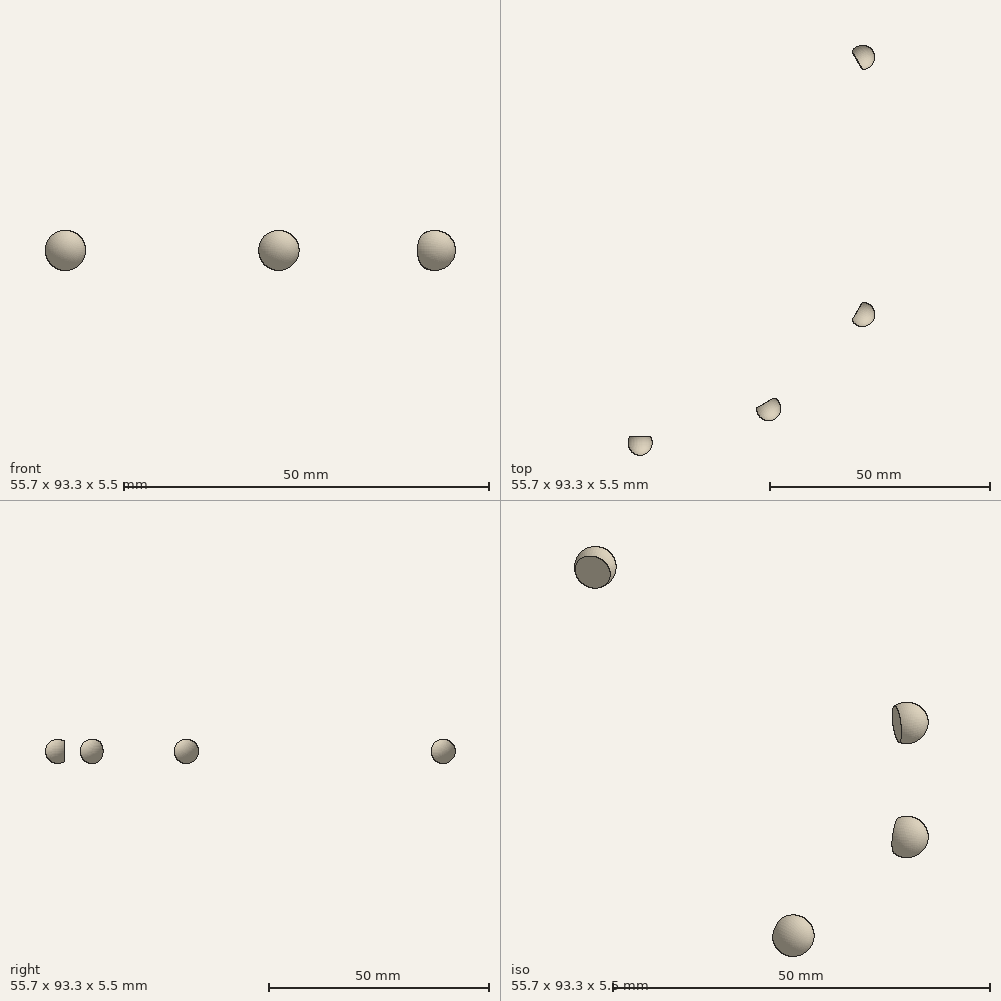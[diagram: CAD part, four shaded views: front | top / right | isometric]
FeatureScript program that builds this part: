
annotation { "Feature Type Name" : "Feature", "Feature Type Description" : "" }
export const myFeature = defineFeature(function(context is Context, id is Id, definition is map)
    precondition{}
    {
        {
            var Q0;
            Q0=qCreatedBy(makeId("Top.planeOp"),FACE);
            var sketch = newSketch(context, id + "F0", { "sketchPlane" : qUnion([Q0])});
            skCircle(sketch, "E0", {"center": v(-1.5, -3.2) * mm, "radius": 60.33 * mm});
            skCircle(sketch, "E1", {"center": v(-1.5, -3.2) * mm, "radius": 57.15 * mm});
            skSolve(sketch);
        }
        {
            var Q0;
            Q0 = qSketchRegion(id + "F0", true);
            extrude(context, id + "F1", {"entities" : qUnion([Q0]), "depth" : 50.8 * mm});
        }
        {
            var Q0;
            Q0=qCreatedBy(makeId("Front.planeOp"),FACE);
            var sketch = newSketch(context, id + "F2", { "sketchPlane" : qUnion([Q0])});
            skLineSegment(sketch, "E2", {"start": v(-61.76, 50.86) * mm, "end": v(58.59, 50.86) * mm});
            skArc(sketch, "E3", {"start": v(-27.24, 27.98) * mm, "mid": v(-10.73, 35.28) * mm, "end": v(-1.59, 50.86) * mm});
            skLineSegment(sketch, "E4", {"start": v(-27.24, 27.98) * mm, "end": v(-71.41, 27.98) * mm});
            skLineSegment(sketch, "E5", {"start": v(-71.41, 27.98) * mm, "end": v(-61.76, 50.86) * mm});
            skSolve(sketch);
        }
        {
            var Q0;
            Q0 = qSketchRegion(id + "F2", true);
            extrude(context, id + "F3", {"entities" : qUnion([Q0]), "operationType" : NewBodyOperationType.REMOVE, "depth" : 68.51 * mm, "hasSecondDirection" : true, "secondDirectionOppositeDirection" : true, "secondDirectionDepth" : 71.55 * mm});
        }
        {
            var Q0;
            Q0=qCreatedBy(makeId("Front.planeOp"),FACE);
            var sketch = newSketch(context, id + "F4", { "sketchPlane" : qUnion([Q0])});
            skLineSegment(sketch, "E6.bottom", {"start": v(-68.64, 54.96) * mm, "end": v(-49.46, 54.96) * mm});
            skLineSegment(sketch, "E6.top", {"start": v(-68.64, 43.72) * mm, "end": v(-49.46, 43.72) * mm});
            skLineSegment(sketch, "E6.left", {"start": v(-68.64, 54.96) * mm, "end": v(-68.64, 43.72) * mm});
            skLineSegment(sketch, "E6.right", {"start": v(-49.46, 54.96) * mm, "end": v(-49.46, 43.72) * mm});
            skSolve(sketch);
        }
        {
            var Q0;
            Q0 = qSketchRegion(id + "F4", true);
            extrude(context, id + "F5", {"entities" : qUnion([Q0]), "operationType" : NewBodyOperationType.REMOVE, "depth" : 25.4 * mm});
        }
        {
            var Q0;
            Q0=qCreatedBy(makeId("Front.planeOp"),FACE);
            var sketch = newSketch(context, id + "F6", { "sketchPlane" : qUnion([Q0])});
            skLineSegment(sketch, "E7", {"start": v(-1.59, 50.56) * mm, "end": v(-1.59, 56.02) * mm});
            skLineSegment(sketch, "E8", {"start": v(-1.59, 56.02) * mm, "end": v(66.65, 56.02) * mm});
            skLineSegment(sketch, "E9", {"start": v(58.85, 27.85) * mm, "end": v(66.65, 56.02) * mm});
            skLineSegment(sketch, "E10", {"start": v(-1.59, 50.56) * mm, "end": v(-1.59, -5.61) * mm});
            skLineSegment(sketch, "E11", {"start": v(58.85, 27.85) * mm, "end": v(65.73, -4.29) * mm});
            skLineSegment(sketch, "E12", {"start": v(-1.59, -5.61) * mm, "end": v(65.73, -4.29) * mm});
            skSolve(sketch);
        }
        {
            var Q0;
            Q0 = qSketchRegion(id + "F6", true);
            extrude(context, id + "F7", {"entities" : qUnion([Q0]), "operationType" : NewBodyOperationType.REMOVE, "oppositeDirection" : true, "depth" : 62.56 * mm, "hasSecondDirection" : true, "secondDirectionOppositeDirection" : false, "secondDirectionDepth" : 75.26 * mm});
        }
        {
            var Q0;
            Q0=makeQuery(id+"F3.boolean.opBoolean","SPLIT",BODY,{"disambiguationData":[OD(1.0)],"derivedFrom":makeQuery(id+"F1.opExtrude","SWEPT_BODY",BODY,{"disambiguationData":[OSD([sQuery(id+"F0.wireOp",EDGE,"E0"),sQuery(id+"F0.wireOp",EDGE,"E1")])]})});
            var Q1;
            Q1=makeQuery(id+"F7.boolean.opBoolean","COPY",FACE,{"disambiguationData":[OD(0.0)],"derivedFrom":makeQuery(id+"F7.opExtrude","SWEPT_FACE",FACE,{"disambiguationData":[OSD([sQuery(id+"F6.wireOp",EDGE,"E7"),sQuery(id+"F6.wireOp",EDGE,"E10")])]})});
            mirror(context, id + "F8", {"operationType" : NewBodyOperationType.ADD, "entities" : qUnion([Q0]), "mirrorPlane" : qUnion([Q1])});
        }
        {
            var Q0;
            Q0=makeQuery(id+"F3.boolean.opBoolean","SPLIT",BODY,{"disambiguationData":[OD(1.0)],"derivedFrom":makeQuery(id+"F1.opExtrude","SWEPT_BODY",BODY,{"disambiguationData":[OSD([sQuery(id+"F0.wireOp",EDGE,"E0"),sQuery(id+"F0.wireOp",EDGE,"E1")])]})});
            var Q1;
            Q1=makeQuery(id+"F3.boolean.opBoolean","INTERSECT",EDGE,{"derivedFrom":[makeQuery(id+"F1.opExtrude","SWEPT_FACE",FACE,{"disambiguationData":[OSD([sQuery(id+"F0.wireOp",EDGE,"E0")])]}),makeQuery(id+"F3.opExtrude","SWEPT_FACE",FACE,{"disambiguationData":[OSD([sQuery(id+"F2.wireOp",EDGE,"E4")])]})]});
            circularPattern(context, id + "F9", {"operationType" : NewBodyOperationType.ADD, "entities" : qUnion([Q0]), "axis" : qUnion([Q1]), "angle" : 30 * degree, "instanceCount" : 6});
        }
        {
            var Q0;
            Q0=qCreatedBy(makeId("Top.planeOp"),FACE);
            cPlane(context, id + "F10", {"entities" : qUnion([Q0]), "cplaneType" : CPlaneType.OFFSET, "offset" : 50.8 * mm, "width" : 152.4 * mm, "height" : 152.4 * mm});
        }
        {
            var Q0;
            Q0=qCreatedBy(id+"F10.planeOp",FACE);
            var sketch = newSketch(context, id + "F11", { "sketchPlane" : qUnion([Q0])});
            skCircle(sketch, "E13", {"center": v(-60.14, -3.32) * mm, "radius": 2.84 * mm});
            skLineSegment(sketch, "E14", {"start": v(-57.3, -3.24) * mm, "end": v(-62.98, -3.24) * mm});
            skSolve(sketch);
        }
        {
            var Q0;
            {var subQ0=sQuery(id+"F11.wireOp",EDGE,"E14");Q0=makeQuery(id+"F11.imprint","IMPRINT",FACE,{"disambiguationData":[TD([[makeQuery(id+"F11.imprint","IMPRINT",EDGE,{"derivedFrom":subQ0}),-1.0]])]});}
            var Q1;
            Q1=sQuery(id+"F11.wireOp",EDGE,"E14");
            revolve(context, id + "F12", {"entities" : qUnion([Q0]), "axis" : qUnion([Q1]), "revolveType" : RevolveType.FULL});
        }
        {
            var Q0;
            Q0=makeQuery(id+"F12.opRevolve","SWEPT_BODY",BODY,{"disambiguationData":[OSD([sQuery(id+"F11.wireOp",EDGE,"E13"),sQuery(id+"F11.wireOp",EDGE,"E14")])]});
            var Q1;
            {var subQ0=sQuery(id+"F0.wireOp",EDGE,"E1");var subQ1=makeQuery(id+"F1.opExtrude","SWEPT_FACE",FACE,{"disambiguationData":[OSD([subQ0])]});var subQ2=subQ1;var subQ3=makeQuery(id+"F8.opPattern","COPY",FACE,{"derivedFrom":subQ2,"instanceName":"1"});var subQ4=sQuery(id+"F0.wireOp",EDGE,"E0");var subQ5=makeQuery(id+"F1.opExtrude","CAP_FACE",FACE,{"disambiguationData":[OSD([subQ4,subQ0])],"isStart":true});var subQ6=subQ5;var subQ7=makeQuery(id+"F8.opPattern","COPY",FACE,{"derivedFrom":subQ6,"instanceName":"1"});var subQ8=makeQuery(id+"F8.boolean.opBoolean","MERGE",FACE,{"derivedFrom":[subQ6,subQ7]});var subQ9=makeQuery(id+"F3.opExtrude","SWEPT_FACE",FACE,{"disambiguationData":[OSD([sQuery(id+"F2.wireOp",EDGE,"E3")])]});var subQ10=makeQuery(id+"F3.boolean.opBoolean","COPY",FACE,{"disambiguationData":[OD(1.0)],"derivedFrom":subQ9});var subQ11=makeQuery(id+"F8.opPattern","COPY",FACE,{"derivedFrom":makeQuery(id+"F3.boolean.opBoolean","COPY",FACE,{"derivedFrom":makeQuery(id+"F3.opExtrude","SWEPT_FACE",FACE,{"disambiguationData":[OSD([sQuery(id+"F2.wireOp",EDGE,"E4")])]})}),"instanceName":"1"});var subQ12=makeQuery(id+"F1.opExtrude","CAP_FACE",FACE,{"disambiguationData":[OSD([subQ4,subQ0])],"isStart":false});Q1=makeQuery(id+"F9.boolean.opBoolean","SPLIT",FACE,{"disambiguationData":[TD([subQ5,subQ12,subQ1,subQ11,makeQuery(id+"F8.opPattern","COPY",FACE,{"derivedFrom":subQ10,"instanceName":"1"}),subQ7,makeQuery(id+"F8.opPattern","COPY",FACE,{"derivedFrom":makeQuery(id+"F7.boolean.opBoolean","SPLIT",FACE,{"disambiguationData":[TD([subQ10])],"derivedFrom":makeQuery(id+"F3.boolean.opBoolean","SPLIT",FACE,{"disambiguationData":[TD([subQ1])],"derivedFrom":subQ12})}),"instanceName":"1"}),makeQuery(id+"F9.opPattern","COPY",FACE,{"derivedFrom":subQ2,"instanceName":"1"}),makeQuery(id+"F9.opPattern","COPY",FACE,{"derivedFrom":subQ11,"instanceName":"1"}),makeQuery(id+"F9.opPattern","COPY",FACE,{"derivedFrom":subQ3,"instanceName":"1"}),makeQuery(id+"F9.opPattern","COPY",FACE,{"derivedFrom":subQ8,"instanceName":"1"}),makeQuery(id+"F9.opPattern","COPY",FACE,{"derivedFrom":subQ2,"instanceName":"2"}),makeQuery(id+"F9.opPattern","COPY",FACE,{"derivedFrom":subQ11,"instanceName":"2"}),makeQuery(id+"F9.opPattern","COPY",FACE,{"derivedFrom":subQ8,"instanceName":"2"}),makeQuery(id+"F9.opPattern","COPY",FACE,{"derivedFrom":subQ2,"instanceName":"3"}),makeQuery(id+"F9.opPattern","COPY",FACE,{"derivedFrom":subQ11,"instanceName":"3"}),makeQuery(id+"F9.opPattern","COPY",FACE,{"derivedFrom":subQ8,"instanceName":"3"}),makeQuery(id+"F9.opPattern","COPY",FACE,{"derivedFrom":subQ2,"instanceName":"4"}),makeQuery(id+"F9.opPattern","COPY",FACE,{"derivedFrom":subQ11,"instanceName":"4"}),makeQuery(id+"F9.opPattern","COPY",FACE,{"derivedFrom":subQ8,"instanceName":"4"}),makeQuery(id+"F9.opPattern","COPY",FACE,{"derivedFrom":subQ2,"instanceName":"5"}),makeQuery(id+"F9.opPattern","COPY",FACE,{"derivedFrom":subQ11,"instanceName":"5"}),makeQuery(id+"F9.opPattern","COPY",FACE,{"derivedFrom":subQ8,"instanceName":"5"})])],"derivedFrom":subQ3});}
            circularPattern(context, id + "F13", {"operationType" : NewBodyOperationType.ADD, "entities" : qUnion([Q0]), "axis" : qUnion([Q1]), "angle" : 30 * degree, "instanceCount" : 12});
        }
        {
            var Q0;
            Q0=qCreatedBy(makeId("Right.planeOp"),FACE);
            cPlane(context, id + "F14", {"entities" : qUnion([Q0]), "cplaneType" : CPlaneType.OFFSET, "offset" : 1.65 * mm, "oppositeDirection" : true, "width" : 152.4 * mm, "height" : 152.4 * mm});
        }
        {
            var Q0;
            Q0=qCreatedBy(id+"F14.planeOp",FACE);
            var sketch = newSketch(context, id + "F15", { "sketchPlane" : qUnion([Q0])});
            skLineSegment(sketch, "E15", {"start": v(-3.04, 29) * mm, "end": v(-13.92, 18.12) * mm});
            skLineSegment(sketch, "E16", {"start": v(-3.04, 29) * mm, "end": v(7.83, 18.12) * mm});
            skLineSegment(sketch, "E17", {"start": v(-13.92, 18.12) * mm, "end": v(-3.04, 7.25) * mm});
            skLineSegment(sketch, "E18", {"start": v(7.83, 18.12) * mm, "end": v(-3.04, 7.25) * mm});
            skLineSegment(sketch, "E19", {"start": v(-3.04, 29) * mm, "end": v(-3.04, 7.25) * mm});
            skLineSegment(sketch, "E20", {"start": v(-13.92, 18.12) * mm, "end": v(7.83, 18.12) * mm});
            skSolve(sketch);
        }
        {
            var Q0;
            Q0 = qSketchRegion(id + "F15", true);
            extrude(context, id + "F16", {"entities" : qUnion([Q0]), "depth" : 60.96 * mm, "hasSecondDirection" : true, "secondDirectionOppositeDirection" : true, "secondDirectionDepth" : 60.96 * mm});
        }
        {
            var Q0;
            {var subQ0=makeQuery(id+"F1.opExtrude","CAP_FACE",FACE,{"disambiguationData":[OSD([sQuery(id+"F0.wireOp",EDGE,"E0"),sQuery(id+"F0.wireOp",EDGE,"E1")])],"isStart":true});var subQ1=makeQuery(id+"F8.boolean.opBoolean","MERGE",FACE,{"derivedFrom":[subQ0,makeQuery(id+"F8.opPattern","COPY",FACE,{"derivedFrom":subQ0,"instanceName":"1"})]});Q0=makeQuery(id+"F9.boolean.opBoolean","MERGE",FACE,{"derivedFrom":[subQ1,makeQuery(id+"F9.opPattern","COPY",FACE,{"derivedFrom":subQ1,"instanceName":"1"}),makeQuery(id+"F9.opPattern","COPY",FACE,{"derivedFrom":subQ1,"instanceName":"2"}),makeQuery(id+"F9.opPattern","COPY",FACE,{"derivedFrom":subQ1,"instanceName":"3"}),makeQuery(id+"F9.opPattern","COPY",FACE,{"derivedFrom":subQ1,"instanceName":"4"}),makeQuery(id+"F9.opPattern","COPY",FACE,{"derivedFrom":subQ1,"instanceName":"5"})]});}
            var sketch = newSketch(context, id + "F17", { "sketchPlane" : qUnion([Q0])});
            skSolve(sketch);
        }
        {
            var Q0;
            Q0 = qSketchRegion(id + "F17", true);
            var Q1;
            {var subQ0=makeQuery(id+"F1.opExtrude","CAP_EDGE",EDGE,{"disambiguationData":[OSD([sQuery(id+"F0.wireOp",EDGE,"E1")])],"isStart":true});Q1=makeQuery(id+"F17.imprint","IMPRINT",FACE,{"disambiguationData":[TD([[makeQuery(id+"F17.imprint","IMPRINT",EDGE,{"derivedFrom":subQ0}),-1.0]])]});}
            extrude(context, id + "F18", {"entities" : qUnion([Q0, Q1]), "operationType" : NewBodyOperationType.REMOVE, "oppositeDirection" : true, "depth" : 101.6 * mm});
        }
        {
            var Q0;
            Q0=makeQuery(id+"F16.opExtrude","CAP_FACE",FACE,{"disambiguationData":[OSD([sQuery(id+"F15.wireOp",EDGE,"E15"),sQuery(id+"F15.wireOp",EDGE,"E16"),sQuery(id+"F15.wireOp",EDGE,"E17"),sQuery(id+"F15.wireOp",EDGE,"E18")])],"isStart":true});
            var sketch = newSketch(context, id + "F19", { "sketchPlane" : qUnion([Q0])});
            skLineSegment(sketch, "E21", {"start": v(3.04, 29) * mm, "end": v(3.04, 7.25) * mm});
            skLineSegment(sketch, "E22", {"start": v(-7.83, 18.12) * mm, "end": v(13.92, 18.12) * mm});
            skSolve(sketch);
        }
        {
            var Q0;
            {var subQ3=makeQuery(id+"F16.opExtrude","CAP_EDGE",EDGE,{"disambiguationData":[OSD([sQuery(id+"F15.wireOp",EDGE,"E16")])],"isStart":true});Q0=makeQuery(id+"F19.imprint","IMPRINT",FACE,{"disambiguationData":[TD([[makeQuery(id+"F19.imprint","IMPRINT",EDGE,{"derivedFrom":subQ3}),1.0]])]});}
            cPlane(context, id + "F20", {"entities" : qUnion([Q0]), "cplaneType" : CPlaneType.OFFSET, "offset" : 2.54 * mm, "width" : 152.4 * mm, "height" : 152.4 * mm});
        }
        {
            var Q0;
            Q0=qCreatedBy(id+"F20.planeOp",FACE);
            var sketch = newSketch(context, id + "F21", { "sketchPlane" : qUnion([Q0])});
            skPoint(sketch, "E23", {"position": v(3.07, 18.1) * mm});
            skSolve(sketch);
        }
        {
            var Q1;
            Q1=sQuery(id+"F21.wireOp",VERTEX,"E23");
            var Q2;
            Q2=makeQuery(id+"F16.opExtrude","CAP_FACE",FACE,{"disambiguationData":[OSD([sQuery(id+"F15.wireOp",EDGE,"E15"),sQuery(id+"F15.wireOp",EDGE,"E16"),sQuery(id+"F15.wireOp",EDGE,"E17"),sQuery(id+"F15.wireOp",EDGE,"E18")])],"isStart":true});
            loft(context, id + "F22", {"operationType" : NewBodyOperationType.ADD, "sheetProfilesArray" : [{ "sheetProfileEntities" : qUnion([Q1]) }, { "sheetProfileEntities" : qUnion([Q2]) }]});
        }
        {
            var Q0;
            Q0=makeQuery(id+"F18.boolean.opBoolean","SPLIT",BODY,{"disambiguationData":[OD(0.0)],"derivedFrom":makeQuery(id+"F16.opExtrude","SWEPT_BODY",BODY,{"disambiguationData":[OSD([sQuery(id+"F15.wireOp",EDGE,"E15"),sQuery(id+"F15.wireOp",EDGE,"E16"),sQuery(id+"F15.wireOp",EDGE,"E17"),sQuery(id+"F15.wireOp",EDGE,"E18")])]})});
            var Q1;
            {var subQ0=makeQuery(id+"F1.opExtrude","CAP_EDGE",EDGE,{"disambiguationData":[OSD([sQuery(id+"F0.wireOp",EDGE,"E0")])],"isStart":true});Q1=makeQuery(id+"F9.boolean.opBoolean","MERGE",EDGE,{"derivedFrom":[subQ0,makeQuery(id+"F9.opPattern","COPY",EDGE,{"derivedFrom":subQ0,"instanceName":"1"}),makeQuery(id+"F9.opPattern","COPY",EDGE,{"derivedFrom":subQ0,"instanceName":"2"}),makeQuery(id+"F9.opPattern","COPY",EDGE,{"derivedFrom":subQ0,"instanceName":"3"}),makeQuery(id+"F9.opPattern","COPY",EDGE,{"derivedFrom":subQ0,"instanceName":"4"}),makeQuery(id+"F9.opPattern","COPY",EDGE,{"derivedFrom":subQ0,"instanceName":"5"})]});}
            circularPattern(context, id + "F23", {"entities" : qUnion([Q0]), "axis" : qUnion([Q1]), "angle" : 30 * degree, "instanceCount" : 12});
        }
        {
            var Q0;
            {var subQ0=makeQuery(id+"F1.opExtrude","CAP_FACE",FACE,{"disambiguationData":[OSD([sQuery(id+"F0.wireOp",EDGE,"E0"),sQuery(id+"F0.wireOp",EDGE,"E1")])],"isStart":true});var subQ1=makeQuery(id+"F8.boolean.opBoolean","MERGE",FACE,{"derivedFrom":[subQ0,makeQuery(id+"F8.opPattern","COPY",FACE,{"derivedFrom":subQ0,"instanceName":"1"})]});Q0=makeQuery(id+"F9.boolean.opBoolean","MERGE",FACE,{"derivedFrom":[subQ1,makeQuery(id+"F9.opPattern","COPY",FACE,{"derivedFrom":subQ1,"instanceName":"1"}),makeQuery(id+"F9.opPattern","COPY",FACE,{"derivedFrom":subQ1,"instanceName":"2"}),makeQuery(id+"F9.opPattern","COPY",FACE,{"derivedFrom":subQ1,"instanceName":"3"}),makeQuery(id+"F9.opPattern","COPY",FACE,{"derivedFrom":subQ1,"instanceName":"4"}),makeQuery(id+"F9.opPattern","COPY",FACE,{"derivedFrom":subQ1,"instanceName":"5"})]});}
            var sketch = newSketch(context, id + "F24", { "sketchPlane" : qUnion([Q0])});
            skCircle(sketch, "E24", {"center": v(-1.5, 3.2) * mm, "radius": 56.69 * mm});
            skCircle(sketch, "E25", {"center": v(-1.5, 3.2) * mm, "radius": 58.46 * mm});
            skSolve(sketch);
        }
        {
            var Q0;
            Q0 = qSketchRegion(id + "F24", true);
            extrude(context, id + "F25", {"entities" : qUnion([Q0]), "operationType" : NewBodyOperationType.ADD, "oppositeDirection" : true, "depth" : 30.48 * mm});
        }
    });
